# Revit family: NBS_WallgateLtd_WCFlshngVlves_DFKIT03
name_source: partatom
category: Pipe Accessories
revit_build: Autodesk Revit 2014 (Build: 20130709_2115(x64)
units: mm (PartAtom-declared; Revit-internal decimal feet)

## types (1)
- DFKIT03
    AssetType = Fixed
    BIMObjectName = NBS_WallgateLtd_WCFlushingValves_DFKIT03
    BodyMaterial = Polyamide 66
    CloseOffRating = 0
    Description = Electronic activation WC direct flush valve, with WRAS approval
    DurationUnit = year
    Features = Highly cost effective, highly energy and water efficient
    FlowCoefficient = 0
    FlushingRate = 1.5
    Form = WC flush valve with airbreak
    HasIntegralShutOffDevice = Yes
    IfcExportAs = IfcValveType
    IfcExportType = FLUSHING
    InletConnectionDiameter = 25 mm  [stored 0.082021 ft]
    IntegralAccessoryOptions = WDC Electronic Controllers, PBA Piezo Touch Buttons, PBA-IR Infra-Red Activation Sensors, WVC Flush Valve Cables, VCWC Vitreous China WC's, CWC-100 Wall Hung WC Pans, CWC-150 Anti-Ligature Back-to-Wall WC Pans, CWC-170 Corner Fit Back-to-Wall WC Pan, CWC-80 Back-to-Wall WC Pan
    IsHighPressure = Yes
    ManufacturerName = Wallgate Ltd
    ManufacturerURL = www.wallgate.com
    MinimumPipeLengthVertical = 300 mm
    ModelNumber = DFKIT03
    NBSCertification = www.nationalbimlibrary.com/cert/4i1hahw3
    NBSDescription = WC flushing valves
    NBSReference = 45-35-70/389
    Name = WCFlushingValves_DFKIT03_WallgateLtd
    NominalHeight = 163 mm
    NominalLength = 126 mm
    NominalWidth = 67 mm
    OperationOptions = Piezo touch buttons or infrared sensors
    PipeDiameter = 39 mm
    PipeMaterial = NBS_Concept
    ProductInformation = www.wallgate.com/products/wc-toilet-urinal-flushing-range/electronic-direct-flushing-range
    Size = 25.4
    TestPressure = 10.0
    ThirdPartyCertification = EN 55014, EN 60730-2-8-1, WRAS compliant
    Uniclass2 = 45-31-93/491
    ValveMaterial = NBS_Concept
    ValveMechanism = Unset
    ValveOperation = Other
    Version = 1
    WarrantyDurationParts = 1
    WarrantyDurationUnit = year
    Weight = 1.0 kg
    WorkingPressure = 0

note: [stored X ft] marks values corroborated as IEEE doubles in the binary element streams (Revit-internal decimal feet)

## geometry (parser evidence)
native form markers: Sweep x1
no freeform markers — native parametric forms only
